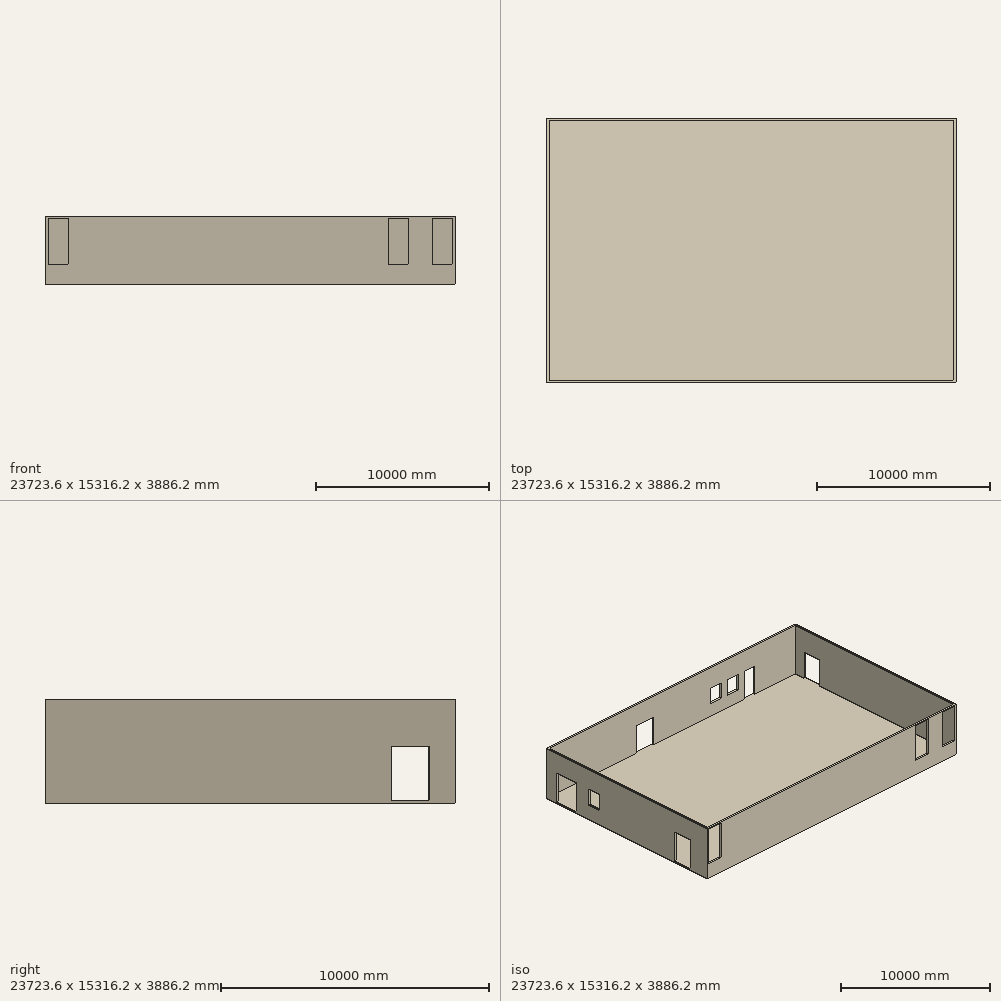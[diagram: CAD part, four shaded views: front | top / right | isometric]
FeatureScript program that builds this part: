
annotation { "Feature Type Name" : "Feature", "Feature Type Description" : "" }
export const myFeature = defineFeature(function(context is Context, id is Id, definition is map)
    precondition{}
    {
        {
            var Q0;
            Q0=qCreatedBy(makeId("Top.planeOp"),FACE);
            var sketch = newSketch(context, id + "F0", { "sketchPlane" : qUnion([Q0])});
            skLineSegment(sketch, "E0.bottom", {"start": v(11709.4, -7505.7) * mm, "end": v(-11709.4, -7505.7) * mm});
            skLineSegment(sketch, "E0.top", {"start": v(11709.4, 7505.7) * mm, "end": v(-11709.4, 7505.7) * mm});
            skLineSegment(sketch, "E0.left", {"start": v(11709.4, -7505.7) * mm, "end": v(11709.4, 7505.7) * mm});
            skLineSegment(sketch, "E0.right", {"start": v(-11709.4, -7505.7) * mm, "end": v(-11709.4, 7505.7) * mm});
            skPoint(sketch, "E0.middle", {"position": v(0, 0) * mm});
            skSolve(sketch);
        }
        {
            var Q0;
            Q0=makeQuery(id+"F0.imprint","IMPRINT",FACE,{"disambiguationData":[TD([[makeQuery(id+"F0.imprint","IMPRINT",EDGE,{"derivedFrom":sQuery(id+"F0.wireOp",EDGE,"E0.bottom")}),-1.0]])]});
            var sketch = newSketch(context, id + "F1", { "sketchPlane" : qUnion([Q0])});
            skLineSegment(sketch, "E1.bottom", {"start": v(11861.8, -7658.1) * mm, "end": v(-11861.8, -7658.1) * mm});
            skLineSegment(sketch, "E1.top", {"start": v(11861.8, 7658.1) * mm, "end": v(-11861.8, 7658.1) * mm});
            skLineSegment(sketch, "E1.left", {"start": v(11861.8, -7658.1) * mm, "end": v(11861.8, 7658.1) * mm});
            skLineSegment(sketch, "E1.right", {"start": v(-11861.8, -7658.1) * mm, "end": v(-11861.8, 7658.1) * mm});
            skPoint(sketch, "E1.middle", {"position": v(0, 0) * mm});
            skSolve(sketch);
        }
        {
            var Q0;
            Q0=makeQuery(id+"F1.imprint","IMPRINT",FACE,{"disambiguationData":[TD([[makeQuery(id+"F1.imprint","IMPRINT",EDGE,{"derivedFrom":sQuery(id+"F1.wireOp",EDGE,"E1.bottom")}),-1.0]])]});
            extrude(context, id + "F2", {"entities" : qUnion([Q0]), "depth" : 3657.6 * mm, "offsetDistance" : 25.4 * mm});
        }
        {
            var Q0;
            Q0=makeQuery(id+"F2.opExtrude","CAP_FACE",FACE,{"disambiguationData":[OSD([sQuery(id+"F0.wireOp",EDGE,"E0.bottom"),sQuery(id+"F0.wireOp",EDGE,"E0.top"),sQuery(id+"F0.wireOp",EDGE,"E0.left"),sQuery(id+"F0.wireOp",EDGE,"E0.right"),sQuery(id+"F1.wireOp",EDGE,"E1.bottom"),sQuery(id+"F1.wireOp",EDGE,"E1.top"),sQuery(id+"F1.wireOp",EDGE,"E1.left"),sQuery(id+"F1.wireOp",EDGE,"E1.right")])],"isStart":true});
            extrude(context, id + "F3", {"entities" : qUnion([Q0]), "operationType" : NewBodyOperationType.ADD, "depth" : 101.6 * mm, "offsetDistance" : 25.4 * mm});
        }
        {
            var Q0;
            {var subQ0=sQuery(id+"F1.wireOp",EDGE,"E1.bottom");Q0=makeQuery(id+"F3.boolean.opBoolean","MERGE",FACE,{"derivedFrom":[makeQuery(id+"F2.opExtrude","SWEPT_FACE",FACE,{"disambiguationData":[OSD([subQ0])]}),makeQuery(id+"F3.opExtrude","SWEPT_FACE",FACE,{"disambiguationData":[OSD([subQ0])]})]});}
            var sketch = newSketch(context, id + "F4", { "sketchPlane" : qUnion([Q0])});
            skLineSegment(sketch, "E2.bottom", {"start": v(-11861.8, -101.6) * mm, "end": v(11861.8, -101.6) * mm});
            skLineSegment(sketch, "E2.top", {"start": v(-11861.8, 3657.6) * mm, "end": v(11861.8, 3657.6) * mm});
            skLineSegment(sketch, "E2.left", {"start": v(-11861.8, -101.6) * mm, "end": v(-11861.8, 3657.6) * mm});
            skLineSegment(sketch, "E2.right", {"start": v(11861.8, -101.6) * mm, "end": v(11861.8, 3657.6) * mm});
            skPoint(sketch, "E3.middle", {"position": v(0, 1778) * mm});
            skPoint(sketch, "E3.middle.positionSnap0", {"position": v(-11861.8, 1778) * mm});
            skPoint(sketch, "E3.centerSnap0", {"position": v(-11861.8, 1778) * mm});
            skLineSegment(sketch, "E4.top", {"start": v(-11861.8, 889) * mm, "end": v(11861.8, 889) * mm});
            skLineSegment(sketch, "E4.left", {"start": v(-11861.8, -101.6) * mm, "end": v(-11861.8, 889) * mm});
            skLineSegment(sketch, "E4.right", {"start": v(11861.8, -101.6) * mm, "end": v(11861.8, 889) * mm});
            skLineSegment(sketch, "E5.top", {"start": v(-11861.8, 3556) * mm, "end": v(11861.8, 3556) * mm});
            skLineSegment(sketch, "E5.left", {"start": v(-11861.8, 3657.6) * mm, "end": v(-11861.8, 3556) * mm});
            skLineSegment(sketch, "E5.right", {"start": v(11861.8, 3657.6) * mm, "end": v(11861.8, 3556) * mm});
            skLineSegment(sketch, "E6.bottom", {"start": v(-11861.8, 889) * mm, "end": v(-11709.4, 889) * mm});
            skLineSegment(sketch, "E6.top", {"start": v(-11861.8, 3556) * mm, "end": v(-11709.4, 3556) * mm});
            skLineSegment(sketch, "E6.left", {"start": v(-11861.8, 889) * mm, "end": v(-11861.8, 3556) * mm});
            skLineSegment(sketch, "E6.right", {"start": v(-11709.4, 889) * mm, "end": v(-11709.4, 3556) * mm});
            skLineSegment(sketch, "E7.bottom", {"start": v(11861.8, 889) * mm, "end": v(11709.4, 889) * mm});
            skLineSegment(sketch, "E7.top", {"start": v(11861.8, 3556) * mm, "end": v(11709.4, 3556) * mm});
            skLineSegment(sketch, "E7.left", {"start": v(11861.8, 889) * mm, "end": v(11861.8, 3556) * mm});
            skLineSegment(sketch, "E7.right", {"start": v(11709.4, 889) * mm, "end": v(11709.4, 3556) * mm});
            skLineSegment(sketch, "E8", {"start": v(-11709.4, 889) * mm, "end": v(-10541, 889) * mm});
            skLineSegment(sketch, "E9", {"start": v(-10541, 889) * mm, "end": v(-10439.4, 889) * mm});
            skLineSegment(sketch, "E10", {"start": v(-10439.4, 889) * mm, "end": v(-9271, 889) * mm});
            skLineSegment(sketch, "E11", {"start": v(-9271, 889) * mm, "end": v(-9169.4, 889) * mm});
            skLineSegment(sketch, "E12", {"start": v(-9169.4, 889) * mm, "end": v(-8001, 889) * mm});
            skLineSegment(sketch, "E13", {"start": v(-8001, 889) * mm, "end": v(-7899.4, 889) * mm});
            skLineSegment(sketch, "E14", {"start": v(-7899.4, 889) * mm, "end": v(-6731, 889) * mm});
            skLineSegment(sketch, "E15", {"start": v(-6731, 889) * mm, "end": v(-6629.4, 889) * mm});
            skLineSegment(sketch, "E16", {"start": v(-6629.4, 889) * mm, "end": v(-5461, 889) * mm});
            skLineSegment(sketch, "E17", {"start": v(-5461, 889) * mm, "end": v(-5359.4, 889) * mm});
            skLineSegment(sketch, "E18", {"start": v(-5359.4, 889) * mm, "end": v(-4191, 889) * mm});
            skLineSegment(sketch, "E19", {"start": v(-4394.36, 889) * mm, "end": v(-4191, 889) * mm});
            skLineSegment(sketch, "E20", {"start": v(-4394.36, 889) * mm, "end": v(-3759.2, 889) * mm});
            skLineSegment(sketch, "E21", {"start": v(-3759.2, 889) * mm, "end": v(-2590.8, 889) * mm});
            skLineSegment(sketch, "E22", {"start": v(-2982.4, 889) * mm, "end": v(-2590.8, 889) * mm});
            skLineSegment(sketch, "E23", {"start": v(-2982.4, 889) * mm, "end": v(-2489.2, 889) * mm});
            skLineSegment(sketch, "E24", {"start": v(-2489.2, 889) * mm, "end": v(-1320.8, 889) * mm});
            skLineSegment(sketch, "E25", {"start": v(-1320.8, 889) * mm, "end": v(-1219.2, 889) * mm});
            skLineSegment(sketch, "E26", {"start": v(-1219.2, 889) * mm, "end": v(-50.8, 889) * mm});
            skLineSegment(sketch, "E27", {"start": v(-50.8, 889) * mm, "end": v(50.8, 889) * mm});
            skLineSegment(sketch, "E28", {"start": v(50.8, 889) * mm, "end": v(1219.2, 889) * mm});
            skLineSegment(sketch, "E29", {"start": v(1219.2, 889) * mm, "end": v(1320.8, 889) * mm});
            skLineSegment(sketch, "E30", {"start": v(1320.8, 889) * mm, "end": v(2489.2, 889) * mm});
            skLineSegment(sketch, "E31", {"start": v(2489.2, 889) * mm, "end": v(2590.8, 889) * mm});
            skLineSegment(sketch, "E32", {"start": v(2590.8, 889) * mm, "end": v(3759.2, 889) * mm});
            skLineSegment(sketch, "E33", {"start": v(3759.2, 889) * mm, "end": v(4191, 889) * mm});
            skLineSegment(sketch, "E34", {"start": v(4191, 889) * mm, "end": v(5359.4, 889) * mm});
            skLineSegment(sketch, "E35", {"start": v(5461, 889) * mm, "end": v(11709.4, 889) * mm});
            skLineSegment(sketch, "E36", {"start": v(5461, 889) * mm, "end": v(6629.4, 889) * mm});
            skLineSegment(sketch, "E37", {"start": v(6629.4, 889) * mm, "end": v(6731, 889) * mm});
            skLineSegment(sketch, "E38", {"start": v(6731, 889) * mm, "end": v(7899.4, 889) * mm});
            skLineSegment(sketch, "E39", {"start": v(7899.4, 889) * mm, "end": v(8585.2, 889) * mm});
            skLineSegment(sketch, "E40", {"start": v(8001, 889) * mm, "end": v(8585.2, 889) * mm});
            skLineSegment(sketch, "E41", {"start": v(8001, 889) * mm, "end": v(9169.4, 889) * mm});
            skLineSegment(sketch, "E42", {"start": v(9169.4, 889) * mm, "end": v(9271, 889) * mm});
            skLineSegment(sketch, "E43", {"start": v(9271, 889) * mm, "end": v(10439.4, 889) * mm});
            skLineSegment(sketch, "E44", {"start": v(10439.4, 889) * mm, "end": v(10541, 889) * mm});
            skLineSegment(sketch, "E45", {"start": v(10541, 889) * mm, "end": v(11709.4, 889) * mm});
            skLineSegment(sketch, "E46", {"start": v(11455.4, 889) * mm, "end": v(11709.4, 889) * mm});
            skLineSegment(sketch, "E47.left", {"start": v(11709.4, 889) * mm, "end": v(11709.4, 889) * mm});
            skLineSegment(sketch, "E47.right", {"start": v(11455.4, 889) * mm, "end": v(11455.4, 889) * mm});
            skLineSegment(sketch, "E48.left", {"start": v(10439.4, 889) * mm, "end": v(10439.4, 889) * mm});
            skLineSegment(sketch, "E48.right", {"start": v(10541, 889) * mm, "end": v(10541, 889) * mm});
            skLineSegment(sketch, "E49.bottom", {"start": v(10541, 889) * mm, "end": v(10439.4, 889) * mm});
            skLineSegment(sketch, "E49.top", {"start": v(10541, 3556) * mm, "end": v(10439.4, 3556) * mm});
            skLineSegment(sketch, "E49.left", {"start": v(10541, 889) * mm, "end": v(10541, 3556) * mm});
            skLineSegment(sketch, "E49.right", {"start": v(10439.4, 889) * mm, "end": v(10439.4, 3556) * mm});
            skLineSegment(sketch, "E50.bottom", {"start": v(9271, 889) * mm, "end": v(9169.4, 889) * mm});
            skLineSegment(sketch, "E50.top", {"start": v(9271, 3556) * mm, "end": v(9169.4, 3556) * mm});
            skLineSegment(sketch, "E50.left", {"start": v(9271, 889) * mm, "end": v(9271, 3556) * mm});
            skLineSegment(sketch, "E50.right", {"start": v(9169.4, 889) * mm, "end": v(9169.4, 3556) * mm});
            skLineSegment(sketch, "E51.bottom", {"start": v(8001, 889) * mm, "end": v(7899.4, 889) * mm});
            skLineSegment(sketch, "E51.top", {"start": v(8001, 3556) * mm, "end": v(7899.4, 3556) * mm});
            skLineSegment(sketch, "E51.left", {"start": v(8001, 889) * mm, "end": v(8001, 3556) * mm});
            skLineSegment(sketch, "E51.right", {"start": v(7899.4, 889) * mm, "end": v(7899.4, 3556) * mm});
            skLineSegment(sketch, "E52.bottom", {"start": v(6731, 889) * mm, "end": v(6629.4, 889) * mm});
            skLineSegment(sketch, "E52.top", {"start": v(6731, 3556) * mm, "end": v(6629.4, 3556) * mm});
            skLineSegment(sketch, "E52.left", {"start": v(6731, 889) * mm, "end": v(6731, 3556) * mm});
            skLineSegment(sketch, "E52.right", {"start": v(6629.4, 889) * mm, "end": v(6629.4, 3556) * mm});
            skLineSegment(sketch, "E53.bottom", {"start": v(5461, 889) * mm, "end": v(5359.4, 889) * mm});
            skLineSegment(sketch, "E53.top", {"start": v(5461, 3556) * mm, "end": v(5359.4, 3556) * mm});
            skLineSegment(sketch, "E53.left", {"start": v(5461, 889) * mm, "end": v(5461, 3556) * mm});
            skLineSegment(sketch, "E53.right", {"start": v(5359.4, 889) * mm, "end": v(5359.4, 3556) * mm});
            skLineSegment(sketch, "E54.bottom", {"start": v(4191, 889) * mm, "end": v(3759.2, 889) * mm});
            skLineSegment(sketch, "E54.top", {"start": v(4191, 889) * mm, "end": v(3759.2, 889) * mm});
            skLineSegment(sketch, "E54.left", {"start": v(4191, 889) * mm, "end": v(4191, 889) * mm});
            skLineSegment(sketch, "E54.right", {"start": v(3759.2, 889) * mm, "end": v(3759.2, 889) * mm});
            skLineSegment(sketch, "E55.top", {"start": v(4191, 3556) * mm, "end": v(3759.2, 3556) * mm});
            skLineSegment(sketch, "E55.left", {"start": v(4191, 889) * mm, "end": v(4191, 3556) * mm});
            skLineSegment(sketch, "E55.right", {"start": v(3759.2, 889) * mm, "end": v(3759.2, 3556) * mm});
            skLineSegment(sketch, "E56.bottom", {"start": v(2590.8, 889) * mm, "end": v(2489.2, 889) * mm});
            skLineSegment(sketch, "E56.top", {"start": v(2590.8, 3556) * mm, "end": v(2489.2, 3556) * mm});
            skLineSegment(sketch, "E56.left", {"start": v(2590.8, 889) * mm, "end": v(2590.8, 3556) * mm});
            skLineSegment(sketch, "E56.right", {"start": v(2489.2, 889) * mm, "end": v(2489.2, 3556) * mm});
            skLineSegment(sketch, "E57.bottom", {"start": v(1320.8, 889) * mm, "end": v(1219.2, 889) * mm});
            skLineSegment(sketch, "E57.top", {"start": v(1320.8, 889) * mm, "end": v(1219.2, 889) * mm});
            skLineSegment(sketch, "E57.left", {"start": v(1320.8, 889) * mm, "end": v(1320.8, 889) * mm});
            skLineSegment(sketch, "E57.right", {"start": v(1219.2, 889) * mm, "end": v(1219.2, 889) * mm});
            skLineSegment(sketch, "E58.top", {"start": v(1320.8, 3556) * mm, "end": v(1219.2, 3556) * mm});
            skLineSegment(sketch, "E58.left", {"start": v(1320.8, 889) * mm, "end": v(1320.8, 3556) * mm});
            skLineSegment(sketch, "E58.right", {"start": v(1219.2, 889) * mm, "end": v(1219.2, 3556) * mm});
            skLineSegment(sketch, "E59.bottom", {"start": v(50.8, 889) * mm, "end": v(-50.8, 889) * mm});
            skLineSegment(sketch, "E59.top", {"start": v(50.8, 3556) * mm, "end": v(-50.8, 3556) * mm});
            skLineSegment(sketch, "E59.left", {"start": v(50.8, 889) * mm, "end": v(50.8, 3556) * mm});
            skLineSegment(sketch, "E59.right", {"start": v(-50.8, 889) * mm, "end": v(-50.8, 3556) * mm});
            skLineSegment(sketch, "E60.bottom", {"start": v(-1219.2, 889) * mm, "end": v(-1320.8, 889) * mm});
            skLineSegment(sketch, "E60.top", {"start": v(-1219.2, 3556) * mm, "end": v(-1320.8, 3556) * mm});
            skLineSegment(sketch, "E60.left", {"start": v(-1219.2, 889) * mm, "end": v(-1219.2, 3556) * mm});
            skLineSegment(sketch, "E60.right", {"start": v(-1320.8, 889) * mm, "end": v(-1320.8, 3556) * mm});
            skLineSegment(sketch, "E61.bottom", {"start": v(-2489.2, 889) * mm, "end": v(-2590.8, 889) * mm});
            skLineSegment(sketch, "E61.top", {"start": v(-2489.2, 3556) * mm, "end": v(-2590.8, 3556) * mm});
            skLineSegment(sketch, "E61.left", {"start": v(-2489.2, 889) * mm, "end": v(-2489.2, 3556) * mm});
            skLineSegment(sketch, "E61.right", {"start": v(-2590.8, 889) * mm, "end": v(-2590.8, 3556) * mm});
            skLineSegment(sketch, "E62.bottom", {"start": v(-3759.2, 889) * mm, "end": v(-4191, 889) * mm});
            skLineSegment(sketch, "E62.top", {"start": v(-3759.2, 3556) * mm, "end": v(-4191, 3556) * mm});
            skLineSegment(sketch, "E62.left", {"start": v(-3759.2, 889) * mm, "end": v(-3759.2, 3556) * mm});
            skLineSegment(sketch, "E62.right", {"start": v(-4191, 889) * mm, "end": v(-4191, 3556) * mm});
            skLineSegment(sketch, "E63.top", {"start": v(-5461, 3556) * mm, "end": v(-5359.4, 3556) * mm});
            skLineSegment(sketch, "E63.left", {"start": v(-5461, 889) * mm, "end": v(-5461, 3556) * mm});
            skLineSegment(sketch, "E63.right", {"start": v(-5359.4, 889) * mm, "end": v(-5359.4, 3556) * mm});
            skLineSegment(sketch, "E64.bottom", {"start": v(-6629.4, 889) * mm, "end": v(-6731, 889) * mm});
            skLineSegment(sketch, "E64.top", {"start": v(-6629.4, 3556) * mm, "end": v(-6731, 3556) * mm});
            skLineSegment(sketch, "E64.left", {"start": v(-6629.4, 889) * mm, "end": v(-6629.4, 3556) * mm});
            skLineSegment(sketch, "E64.right", {"start": v(-6731, 889) * mm, "end": v(-6731, 3556) * mm});
            skLineSegment(sketch, "E65.bottom", {"start": v(-7899.4, 889) * mm, "end": v(-8001, 889) * mm});
            skLineSegment(sketch, "E65.top", {"start": v(-7899.4, 3556) * mm, "end": v(-8001, 3556) * mm});
            skLineSegment(sketch, "E65.left", {"start": v(-7899.4, 889) * mm, "end": v(-7899.4, 3556) * mm});
            skLineSegment(sketch, "E65.right", {"start": v(-8001, 889) * mm, "end": v(-8001, 3556) * mm});
            skLineSegment(sketch, "E66.bottom", {"start": v(-9169.4, 889) * mm, "end": v(-9271, 889) * mm});
            skLineSegment(sketch, "E66.top", {"start": v(-9169.4, 3556) * mm, "end": v(-9271, 3556) * mm});
            skLineSegment(sketch, "E66.left", {"start": v(-9169.4, 889) * mm, "end": v(-9169.4, 3556) * mm});
            skLineSegment(sketch, "E66.right", {"start": v(-9271, 889) * mm, "end": v(-9271, 3556) * mm});
            skLineSegment(sketch, "E67.bottom", {"start": v(-10439.4, 889) * mm, "end": v(-10541, 889) * mm});
            skLineSegment(sketch, "E67.top", {"start": v(-10439.4, 3556) * mm, "end": v(-10541, 3556) * mm});
            skLineSegment(sketch, "E67.left", {"start": v(-10439.4, 889) * mm, "end": v(-10439.4, 3556) * mm});
            skLineSegment(sketch, "E67.right", {"start": v(-10541, 889) * mm, "end": v(-10541, 3556) * mm});
            skSolve(sketch);
        }
        {
            var Q0;
            {var subQ0=sQuery(id+"F1.wireOp",EDGE,"E1.top");Q0=makeQuery(id+"F3.boolean.opBoolean","MERGE",FACE,{"derivedFrom":[makeQuery(id+"F2.opExtrude","SWEPT_FACE",FACE,{"disambiguationData":[OSD([subQ0])]}),makeQuery(id+"F3.opExtrude","SWEPT_FACE",FACE,{"disambiguationData":[OSD([subQ0])]})]});}
            var sketch = newSketch(context, id + "F5", { "sketchPlane" : qUnion([Q0])});
            skLineSegment(sketch, "E68", {"start": v(-11861.8, -101.6) * mm, "end": v(-11811, -101.6) * mm});
            skLineSegment(sketch, "E69", {"start": v(-11861.8, -101.6) * mm, "end": v(-7823.2, -101.6) * mm});
            skLineSegment(sketch, "E70", {"start": v(-7823.2, -101.6) * mm, "end": v(-6832.6, -101.6) * mm});
            skLineSegment(sketch, "E71", {"start": v(-6832.6, -101.6) * mm, "end": v(-6223, -101.6) * mm});
            skLineSegment(sketch, "E72", {"start": v(-6223, -101.6) * mm, "end": v(-5232.4, -101.6) * mm});
            skLineSegment(sketch, "E73", {"start": v(-5232.4, -101.6) * mm, "end": v(-4622.8, -101.6) * mm});
            skLineSegment(sketch, "E74", {"start": v(-4622.8, -101.6) * mm, "end": v(-3632.2, -101.6) * mm});
            skLineSegment(sketch, "E75", {"start": v(-3632.2, -101.6) * mm, "end": v(1803.4, -101.6) * mm});
            skLineSegment(sketch, "E76", {"start": v(11861.8, -101.6) * mm, "end": v(10871.2, -101.6) * mm});
            skLineSegment(sketch, "E77", {"start": v(10871.2, -101.6) * mm, "end": v(9855.2, -101.6) * mm});
            skLineSegment(sketch, "E78", {"start": v(9855.2, -101.6) * mm, "end": v(7010.4, -101.6) * mm});
            skLineSegment(sketch, "E79", {"start": v(7010.4, -101.6) * mm, "end": v(5994.4, -101.6) * mm});
            skLineSegment(sketch, "E80", {"start": v(1803.4, -101.6) * mm, "end": v(3429, -101.6) * mm});
            skLineSegment(sketch, "E81", {"start": v(-11811, -101.6) * mm, "end": v(-10795, -101.6) * mm});
            skLineSegment(sketch, "E82.top", {"start": v(-11811, 2082.8) * mm, "end": v(-10795, 2082.8) * mm});
            skLineSegment(sketch, "E82.left", {"start": v(-11811, -101.6) * mm, "end": v(-11811, 2082.8) * mm});
            skLineSegment(sketch, "E82.right", {"start": v(-10795, -101.6) * mm, "end": v(-10795, 2082.8) * mm});
            skLineSegment(sketch, "E83.top", {"start": v(-7823.2, 2082.8) * mm, "end": v(-6832.6, 2082.8) * mm});
            skLineSegment(sketch, "E83.left", {"start": v(-7823.2, -101.6) * mm, "end": v(-7823.2, 2082.8) * mm});
            skLineSegment(sketch, "E83.right", {"start": v(-6832.6, -101.6) * mm, "end": v(-6832.6, 2082.8) * mm});
            skLineSegment(sketch, "E84.top", {"start": v(-6223, 889) * mm, "end": v(-5232.4, 889) * mm});
            skLineSegment(sketch, "E84.left", {"start": v(-6223, -101.6) * mm, "end": v(-6223, 889) * mm});
            skLineSegment(sketch, "E84.right", {"start": v(-5232.4, -101.6) * mm, "end": v(-5232.4, 889) * mm});
            skLineSegment(sketch, "E85.top", {"start": v(-6223, 2082.8) * mm, "end": v(-5232.4, 2082.8) * mm});
            skLineSegment(sketch, "E85.left", {"start": v(-6223, 889) * mm, "end": v(-6223, 2082.8) * mm});
            skLineSegment(sketch, "E85.right", {"start": v(-5232.4, 889) * mm, "end": v(-5232.4, 2082.8) * mm});
            skLineSegment(sketch, "E86.top", {"start": v(-4622.8, 889) * mm, "end": v(-3632.2, 889) * mm});
            skLineSegment(sketch, "E86.left", {"start": v(-4622.8, -101.6) * mm, "end": v(-4622.8, 889) * mm});
            skLineSegment(sketch, "E86.right", {"start": v(-3632.2, -101.6) * mm, "end": v(-3632.2, 889) * mm});
            skLineSegment(sketch, "E87.top", {"start": v(-4622.8, 2082.8) * mm, "end": v(-3632.2, 2082.8) * mm});
            skLineSegment(sketch, "E87.left", {"start": v(-4622.8, 889) * mm, "end": v(-4622.8, 2082.8) * mm});
            skLineSegment(sketch, "E87.right", {"start": v(-3632.2, 889) * mm, "end": v(-3632.2, 2082.8) * mm});
            skLineSegment(sketch, "E88.top", {"start": v(1803.4, 2032) * mm, "end": v(3429, 2032) * mm});
            skLineSegment(sketch, "E88.left", {"start": v(1803.4, -101.6) * mm, "end": v(1803.4, 2032) * mm});
            skLineSegment(sketch, "E88.right", {"start": v(3429, -101.6) * mm, "end": v(3429, 2032) * mm});
            skLineSegment(sketch, "E89.bottom", {"start": v(5994.4, -101.6) * mm, "end": v(7010.4, -101.6) * mm});
            skLineSegment(sketch, "E89.top", {"start": v(5994.4, 2387.6) * mm, "end": v(7010.4, 2387.6) * mm});
            skLineSegment(sketch, "E89.left", {"start": v(5994.4, -101.6) * mm, "end": v(5994.4, 2387.6) * mm});
            skLineSegment(sketch, "E89.right", {"start": v(7010.4, -101.6) * mm, "end": v(7010.4, 2387.6) * mm});
            skLineSegment(sketch, "E90.bottom", {"start": v(9855.2, -101.6) * mm, "end": v(10871.2, -101.6) * mm});
            skLineSegment(sketch, "E90.top", {"start": v(9855.2, 2387.6) * mm, "end": v(10871.2, 2387.6) * mm});
            skLineSegment(sketch, "E90.left", {"start": v(9855.2, -101.6) * mm, "end": v(9855.2, 2387.6) * mm});
            skLineSegment(sketch, "E90.right", {"start": v(10871.2, -101.6) * mm, "end": v(10871.2, 2387.6) * mm});
            skSolve(sketch);
        }
        {
            var Q0;
            Q0=makeQuery(id+"F5.imprint","IMPRINT",FACE,{"disambiguationData":[TD([[makeQuery(id+"F5.imprint","IMPRINT",EDGE,{"derivedFrom":sQuery(id+"F5.wireOp",EDGE,"E90.bottom")}),1.0]])]});
            var Q1;
            Q1=makeQuery(id+"F5.imprint","IMPRINT",FACE,{"disambiguationData":[TD([[makeQuery(id+"F5.imprint","IMPRINT",EDGE,{"derivedFrom":sQuery(id+"F5.wireOp",EDGE,"E89.bottom")}),1.0]])]});
            var Q2;
            Q2=makeQuery(id+"F5.imprint","IMPRINT",FACE,{"disambiguationData":[TD([[makeQuery(id+"F5.imprint","IMPRINT",EDGE,{"derivedFrom":sQuery(id+"F5.wireOp",EDGE,"E80")}),1.0]])]});
            var Q3;
            Q3=makeQuery(id+"F5.imprint","IMPRINT",FACE,{"disambiguationData":[TD([[makeQuery(id+"F5.imprint","IMPRINT",EDGE,{"derivedFrom":sQuery(id+"F5.wireOp",EDGE,"E86.top")}),1.0]])]});
            var Q4;
            Q4=makeQuery(id+"F5.imprint","IMPRINT",FACE,{"disambiguationData":[TD([[makeQuery(id+"F5.imprint","IMPRINT",EDGE,{"derivedFrom":sQuery(id+"F5.wireOp",EDGE,"E84.top")}),1.0]])]});
            var Q5;
            Q5=makeQuery(id+"F5.imprint","IMPRINT",FACE,{"disambiguationData":[TD([[makeQuery(id+"F5.imprint","IMPRINT",EDGE,{"derivedFrom":sQuery(id+"F5.wireOp",EDGE,"E70")}),1.0]])]});
            var Q6;
            Q6=makeQuery(id+"F5.imprint","IMPRINT",FACE,{"disambiguationData":[TD([[makeQuery(id+"F5.imprint","IMPRINT",EDGE,{"derivedFrom":sQuery(id+"F5.wireOp",EDGE,"E81")}),1.0]])]});
            extrude(context, id + "F6", {"entities" : qUnion([Q0, Q1, Q2, Q3, Q4, Q5, Q6]), "operationType" : NewBodyOperationType.REMOVE, "oppositeDirection" : true, "depth" : 304.8 * mm, "offsetDistance" : 25.4 * mm});
        }
        {
            var Q0;
            {var subQ0=sQuery(id+"F4.wireOp",EDGE,"E6.right");Q0=makeQuery(id+"F4.imprint","IMPRINT",FACE,{"disambiguationData":[TD([[makeQuery(id+"F4.imprint","IMPRINT",EDGE,{"derivedFrom":subQ0}),-1.0]])]});}
            var Q1;
            Q1=makeQuery(id+"F4.imprint","IMPRINT",FACE,{"disambiguationData":[TD([[makeQuery(id+"F4.imprint","IMPRINT",EDGE,{"derivedFrom":sQuery(id+"F4.wireOp",EDGE,"E10")}),1.0]])]});
            var Q2;
            Q2=makeQuery(id+"F4.imprint","IMPRINT",FACE,{"disambiguationData":[TD([[makeQuery(id+"F4.imprint","IMPRINT",EDGE,{"derivedFrom":sQuery(id+"F4.wireOp",EDGE,"E12")}),1.0]])]});
            var Q3;
            Q3=makeQuery(id+"F4.imprint","IMPRINT",FACE,{"disambiguationData":[TD([[makeQuery(id+"F4.imprint","IMPRINT",EDGE,{"derivedFrom":sQuery(id+"F4.wireOp",EDGE,"E14")}),1.0]])]});
            var Q4;
            Q4=makeQuery(id+"F4.imprint","IMPRINT",FACE,{"disambiguationData":[TD([[makeQuery(id+"F4.imprint","IMPRINT",EDGE,{"derivedFrom":sQuery(id+"F4.wireOp",EDGE,"E16")}),1.0]])]});
            var Q5;
            Q5=makeQuery(id+"F4.imprint","IMPRINT",FACE,{"disambiguationData":[TD([[makeQuery(id+"F4.imprint","IMPRINT",EDGE,{"derivedFrom":sQuery(id+"F4.wireOp",EDGE,"E18")}),1.0]])]});
            var Q6;
            Q6=makeQuery(id+"F4.imprint","IMPRINT",FACE,{"disambiguationData":[TD([[makeQuery(id+"F4.imprint","IMPRINT",EDGE,{"derivedFrom":sQuery(id+"F4.wireOp",EDGE,"E21")}),1.0]])]});
            var Q7;
            Q7=makeQuery(id+"F4.imprint","IMPRINT",FACE,{"disambiguationData":[TD([[makeQuery(id+"F4.imprint","IMPRINT",EDGE,{"derivedFrom":sQuery(id+"F4.wireOp",EDGE,"E24")}),1.0]])]});
            var Q8;
            Q8=makeQuery(id+"F4.imprint","IMPRINT",FACE,{"disambiguationData":[TD([[makeQuery(id+"F4.imprint","IMPRINT",EDGE,{"derivedFrom":sQuery(id+"F4.wireOp",EDGE,"E26")}),1.0]])]});
            var Q9;
            Q9=makeQuery(id+"F4.imprint","IMPRINT",FACE,{"disambiguationData":[TD([[makeQuery(id+"F4.imprint","IMPRINT",EDGE,{"derivedFrom":sQuery(id+"F4.wireOp",EDGE,"E28")}),1.0]])]});
            var Q10;
            Q10=makeQuery(id+"F4.imprint","IMPRINT",FACE,{"disambiguationData":[TD([[makeQuery(id+"F4.imprint","IMPRINT",EDGE,{"derivedFrom":sQuery(id+"F4.wireOp",EDGE,"E30")}),1.0]])]});
            var Q11;
            Q11=makeQuery(id+"F4.imprint","IMPRINT",FACE,{"disambiguationData":[TD([[makeQuery(id+"F4.imprint","IMPRINT",EDGE,{"derivedFrom":sQuery(id+"F4.wireOp",EDGE,"E32")}),1.0]])]});
            var Q12;
            Q12=makeQuery(id+"F4.imprint","IMPRINT",FACE,{"disambiguationData":[TD([[makeQuery(id+"F4.imprint","IMPRINT",EDGE,{"derivedFrom":sQuery(id+"F4.wireOp",EDGE,"E34")}),1.0]])]});
            var Q13;
            Q13=makeQuery(id+"F4.imprint","IMPRINT",FACE,{"disambiguationData":[TD([[makeQuery(id+"F4.imprint","IMPRINT",EDGE,{"derivedFrom":sQuery(id+"F4.wireOp",EDGE,"E36")}),1.0]])]});
            var Q14;
            Q14=makeQuery(id+"F4.imprint","IMPRINT",FACE,{"disambiguationData":[TD([[makeQuery(id+"F4.imprint","IMPRINT",EDGE,{"derivedFrom":sQuery(id+"F4.wireOp",EDGE,"E38")}),1.0]])]});
            var Q15;
            {var subQ0=sQuery(id+"F4.wireOp",EDGE,"E50.right");Q15=makeQuery(id+"F4.imprint","IMPRINT",FACE,{"disambiguationData":[TD([[makeQuery(id+"F4.imprint","IMPRINT",EDGE,{"derivedFrom":subQ0}),1.0]])]});}
            var Q16;
            Q16=makeQuery(id+"F4.imprint","IMPRINT",FACE,{"disambiguationData":[TD([[makeQuery(id+"F4.imprint","IMPRINT",EDGE,{"derivedFrom":sQuery(id+"F4.wireOp",EDGE,"E43")}),1.0]])]});
            var Q17;
            {var subQ0=sQuery(id+"F4.wireOp",EDGE,"E7.right");Q17=makeQuery(id+"F4.imprint","IMPRINT",FACE,{"disambiguationData":[TD([[makeQuery(id+"F4.imprint","IMPRINT",EDGE,{"derivedFrom":subQ0}),1.0]])]});}
            extrude(context, id + "F7", {"entities" : qUnion([Q0, Q1, Q2, Q3, Q4, Q5, Q6, Q7, Q8, Q9, Q10, Q11, Q12, Q13, Q14, Q15, Q16, Q17]), "operationType" : NewBodyOperationType.REMOVE, "oppositeDirection" : true, "depth" : 304.8 * mm, "offsetDistance" : 25.4 * mm});
        }
        {
            var Q0;
            {var subQ0=sQuery(id+"F1.wireOp",EDGE,"E1.right");Q0=makeQuery(id+"F3.boolean.opBoolean","MERGE",FACE,{"derivedFrom":[makeQuery(id+"F2.opExtrude","SWEPT_FACE",FACE,{"disambiguationData":[OSD([subQ0])]}),makeQuery(id+"F3.opExtrude","SWEPT_FACE",FACE,{"disambiguationData":[OSD([subQ0])]})]});}
            var sketch = newSketch(context, id + "F8", { "sketchPlane" : qUnion([Q0])});
            skLineSegment(sketch, "E91", {"start": v(-7658.1, -101.6) * mm, "end": v(-6667.5, -101.6) * mm});
            skLineSegment(sketch, "E92.bottom", {"start": v(-6667.5, -101.6) * mm, "end": v(-4762.5, -101.6) * mm});
            skLineSegment(sketch, "E92.top", {"start": v(-6667.5, 2133.6) * mm, "end": v(-4762.5, 2133.6) * mm});
            skLineSegment(sketch, "E92.left", {"start": v(-6667.5, -101.6) * mm, "end": v(-6667.5, 2133.6) * mm});
            skLineSegment(sketch, "E92.right", {"start": v(-4762.5, -101.6) * mm, "end": v(-4762.5, 2133.6) * mm});
            skLineSegment(sketch, "E93", {"start": v(-4762.5, -101.6) * mm, "end": v(-3644.9, -101.6) * mm});
            skLineSegment(sketch, "E94.top", {"start": v(-3644.9, -101.6) * mm, "end": v(-3644.9, -101.6) * mm});
            skLineSegment(sketch, "E94.left", {"start": v(-3644.9, -101.6) * mm, "end": v(-3644.9, -101.6) * mm});
            skLineSegment(sketch, "E95.bottom", {"start": v(-3644.9, -101.6) * mm, "end": v(-2654.3, -101.6) * mm});
            skLineSegment(sketch, "E95.top", {"start": v(-3644.9, 889) * mm, "end": v(-2654.3, 889) * mm});
            skLineSegment(sketch, "E95.left", {"start": v(-3644.9, -101.6) * mm, "end": v(-3644.9, 889) * mm});
            skLineSegment(sketch, "E95.right", {"start": v(-2654.3, -101.6) * mm, "end": v(-2654.3, 889) * mm});
            skLineSegment(sketch, "E96.left", {"start": v(-3644.9, 889) * mm, "end": v(-3644.9, 889) * mm});
            skLineSegment(sketch, "E96.right", {"start": v(-2654.3, 889) * mm, "end": v(-2654.3, 889) * mm});
            skLineSegment(sketch, "E97.top", {"start": v(-3644.9, 2133.6) * mm, "end": v(-2654.3, 2133.6) * mm});
            skLineSegment(sketch, "E97.left", {"start": v(-3644.9, 889) * mm, "end": v(-3644.9, 2133.6) * mm});
            skLineSegment(sketch, "E97.right", {"start": v(-2654.3, 889) * mm, "end": v(-2654.3, 2133.6) * mm});
            skLineSegment(sketch, "E98", {"start": v(7658.1, -101.6) * mm, "end": v(6096, -101.6) * mm});
            skLineSegment(sketch, "E99.bottom", {"start": v(6096, -101.6) * mm, "end": v(4572, -101.6) * mm});
            skLineSegment(sketch, "E99.top", {"start": v(6096, 2133.6) * mm, "end": v(4572, 2133.6) * mm});
            skLineSegment(sketch, "E99.left", {"start": v(6096, -101.6) * mm, "end": v(6096, 2133.6) * mm});
            skLineSegment(sketch, "E99.right", {"start": v(4572, -101.6) * mm, "end": v(4572, 2133.6) * mm});
            skSolve(sketch);
        }
        {
            var Q0;
            Q0=makeQuery(id+"F8.imprint","IMPRINT",FACE,{"disambiguationData":[TD([[makeQuery(id+"F8.imprint","IMPRINT",EDGE,{"derivedFrom":sQuery(id+"F8.wireOp",EDGE,"E95.top")}),1.0]])]});
            var Q1;
            Q1=makeQuery(id+"F8.imprint","IMPRINT",FACE,{"disambiguationData":[TD([[makeQuery(id+"F8.imprint","IMPRINT",EDGE,{"derivedFrom":sQuery(id+"F8.wireOp",EDGE,"E92.bottom")}),-1.0]])]});
            extrude(context, id + "F9", {"entities" : qUnion([Q0, Q1]), "operationType" : NewBodyOperationType.REMOVE, "oppositeDirection" : true, "depth" : 304.8 * mm, "offsetDistance" : 25.4 * mm});
        }
        {
            var Q0;
            {var subQ0=sQuery(id+"F0.wireOp",EDGE,"E0.right");var subQ1=sQuery(id+"F0.wireOp",EDGE,"E0.left");var subQ2=sQuery(id+"F0.wireOp",EDGE,"E0.top");var subQ3=sQuery(id+"F0.wireOp",EDGE,"E0.bottom");Q0=makeQuery(id+"FCbTjNU9k0kp0He_1.boolean.opBoolean","MERGE",FACE,{"derivedFrom":[makeQuery(id+"F3.opExtrude","CAP_FACE",FACE,{"disambiguationData":[OSD([subQ3,subQ2,subQ1,subQ0,sQuery(id+"F1.wireOp",EDGE,"E1.bottom"),sQuery(id+"F1.wireOp",EDGE,"E1.top"),sQuery(id+"F1.wireOp",EDGE,"E1.left"),sQuery(id+"F1.wireOp",EDGE,"E1.right")])],"isStart":false}),makeQuery(id+"FCbTjNU9k0kp0He_1.opExtrude","CAP_FACE",FACE,{"disambiguationData":[OSD([subQ3,subQ2,subQ1,subQ0])],"isStart":false})]});}
            var sketch = newSketch(context, id + "F10", { "sketchPlane" : qUnion([Q0])});
            skLineSegment(sketch, "E100.bottom", {"start": v(11861.8, 7658.1) * mm, "end": v(-11861.8, 7658.1) * mm});
            skLineSegment(sketch, "E100.top", {"start": v(11861.8, -7658.1) * mm, "end": v(-11861.8, -7658.1) * mm});
            skLineSegment(sketch, "E100.left", {"start": v(11861.8, 7658.1) * mm, "end": v(11861.8, -7658.1) * mm});
            skLineSegment(sketch, "E100.right", {"start": v(-11861.8, 7658.1) * mm, "end": v(-11861.8, -7658.1) * mm});
            skSolve(sketch);
        }
        {
            var Q0;
            Q0 = qSketchRegion(id + "F10", true);
            extrude(context, id + "F11", {"entities" : qUnion([Q0]), "operationType" : NewBodyOperationType.ADD, "depth" : 127 * mm, "offsetDistance" : 25.4 * mm});
        }
        {
            var Q0;
            {var subQ0=sQuery(id+"F1.wireOp",EDGE,"E1.left");Q0=makeQuery(id+"F11.boolean.opBoolean","MERGE",FACE,{"derivedFrom":[makeQuery(id+"F3.boolean.opBoolean","MERGE",FACE,{"derivedFrom":[makeQuery(id+"F2.opExtrude","SWEPT_FACE",FACE,{"disambiguationData":[OSD([subQ0])]}),makeQuery(id+"F3.opExtrude","SWEPT_FACE",FACE,{"disambiguationData":[OSD([subQ0])]})]}),makeQuery(id+"F11.opExtrude","SWEPT_FACE",FACE,{"disambiguationData":[OSD([sQuery(id+"F10.wireOp",EDGE,"E100.left")])]})]});}
            var sketch = newSketch(context, id + "F12", { "sketchPlane" : qUnion([Q0])});
            skLineSegment(sketch, "E101", {"start": v(7658.1, -228.6) * mm, "end": v(6692.9, -228.6) * mm});
            skLineSegment(sketch, "E102.bottom", {"start": v(6692.9, -228.6) * mm, "end": v(5270.5, -228.6) * mm});
            skLineSegment(sketch, "E102.top", {"start": v(6692.9, 1905) * mm, "end": v(5270.5, 1905) * mm});
            skLineSegment(sketch, "E102.left", {"start": v(6692.9, -228.6) * mm, "end": v(6692.9, 1905) * mm});
            skLineSegment(sketch, "E102.right", {"start": v(5270.5, -228.6) * mm, "end": v(5270.5, 1905) * mm});
            skLineSegment(sketch, "E103.bottom", {"start": v(5270.5, -228.6) * mm, "end": v(6692.9, -228.6) * mm});
            skLineSegment(sketch, "E103.top", {"start": v(5270.5, -228.6) * mm, "end": v(6692.9, -228.6) * mm});
            skLineSegment(sketch, "E103.left", {"start": v(5270.5, -228.6) * mm, "end": v(5270.5, -228.6) * mm});
            skLineSegment(sketch, "E103.right", {"start": v(6692.9, -228.6) * mm, "end": v(6692.9, -228.6) * mm});
            skLineSegment(sketch, "E104.left", {"start": v(5270.5, -228.6) * mm, "end": v(5270.5, -101.6) * mm});
            skLineSegment(sketch, "E104.right", {"start": v(6692.9, -127) * mm, "end": v(6692.9, 0) * mm});
            skLineSegment(sketch, "E105.top", {"start": v(5270.5, -203.2) * mm, "end": v(6692.9, -203.2) * mm});
            skLineSegment(sketch, "E105.left", {"start": v(5270.5, -228.6) * mm, "end": v(5270.5, -203.2) * mm});
            skLineSegment(sketch, "E105.right", {"start": v(6692.9, -228.6) * mm, "end": v(6692.9, -203.2) * mm});
            skSolve(sketch);
        }
        {
            var Q0;
            Q0=makeQuery(id+"F12.imprint","IMPRINT",FACE,{"disambiguationData":[TD([[makeQuery(id+"F12.imprint","IMPRINT",EDGE,{"derivedFrom":sQuery(id+"F12.wireOp",EDGE,"E102.top")}),1.0]])]});
            extrude(context, id + "F13", {"entities" : qUnion([Q0]), "operationType" : NewBodyOperationType.REMOVE, "oppositeDirection" : true, "depth" : 279.4 * mm, "offsetDistance" : 25.4 * mm});
        }
        {
            var Q0;
            Q0=makeQuery(id+"F13.boolean.opBoolean","COPY",FACE,{"derivedFrom":makeQuery(id+"F13.opExtrude","CAP_FACE",FACE,{"disambiguationData":[OSD([sQuery(id+"F12.wireOp",EDGE,"E102.top"),sQuery(id+"F12.wireOp",EDGE,"E102.left"),sQuery(id+"F12.wireOp",EDGE,"E102.right"),sQuery(id+"F12.wireOp",EDGE,"E104.left"),sQuery(id+"F12.wireOp",EDGE,"E104.right"),sQuery(id+"F12.wireOp",EDGE,"E105.top")])],"isStart":false})});
            var sketch = newSketch(context, id + "F14", { "sketchPlane" : qUnion([Q0])});
            skLineSegment(sketch, "E106.bottom", {"start": v(5270.5, -203.2) * mm, "end": v(6692.9, -203.2) * mm});
            skLineSegment(sketch, "E106.top", {"start": v(5270.5, -101.6) * mm, "end": v(6692.9, -101.6) * mm});
            skLineSegment(sketch, "E106.left", {"start": v(5270.5, -203.2) * mm, "end": v(5270.5, -101.6) * mm});
            skLineSegment(sketch, "E106.right", {"start": v(6692.9, -203.2) * mm, "end": v(6692.9, -101.6) * mm});
            skSolve(sketch);
        }
        {
            var Q0;
            Q0=makeQuery(id+"F14.imprint","IMPRINT",FACE,{"disambiguationData":[TD([[makeQuery(id+"F14.imprint","IMPRINT",EDGE,{"derivedFrom":sQuery(id+"F14.wireOp",EDGE,"E106.bottom")}),1.0]])]});
            var Q1;
            {var subQ0=sQuery(id+"F1.wireOp",EDGE,"E1.left");Q1=makeQuery(id+"F11.boolean.opBoolean","MERGE",FACE,{"derivedFrom":[makeQuery(id+"F3.boolean.opBoolean","MERGE",FACE,{"derivedFrom":[makeQuery(id+"F2.opExtrude","SWEPT_FACE",FACE,{"disambiguationData":[OSD([subQ0])]}),makeQuery(id+"F3.opExtrude","SWEPT_FACE",FACE,{"disambiguationData":[OSD([subQ0])]})]}),makeQuery(id+"F11.opExtrude","SWEPT_FACE",FACE,{"disambiguationData":[OSD([sQuery(id+"F10.wireOp",EDGE,"E100.left")])]})]});}
            extrude(context, id + "F15", {"entities" : qUnion([Q0]), "operationType" : NewBodyOperationType.ADD, "endBound" : BoundingType.UP_TO_SURFACE, "depth" : 25.4 * mm, "endBoundEntityFace" : qUnion([Q1]), "offsetDistance" : 25.4 * mm});
        }
        {
            var Q0;
            Q0=makeQuery(id+"F8.imprint","IMPRINT",FACE,{"disambiguationData":[TD([[makeQuery(id+"F8.imprint","IMPRINT",EDGE,{"derivedFrom":sQuery(id+"F8.wireOp",EDGE,"E99.bottom")}),-1.0]])]});
            extrude(context, id + "F16", {"entities" : qUnion([Q0]), "operationType" : NewBodyOperationType.REMOVE, "oppositeDirection" : true, "depth" : 304.8 * mm, "offsetDistance" : 25.4 * mm});
        }
    });
